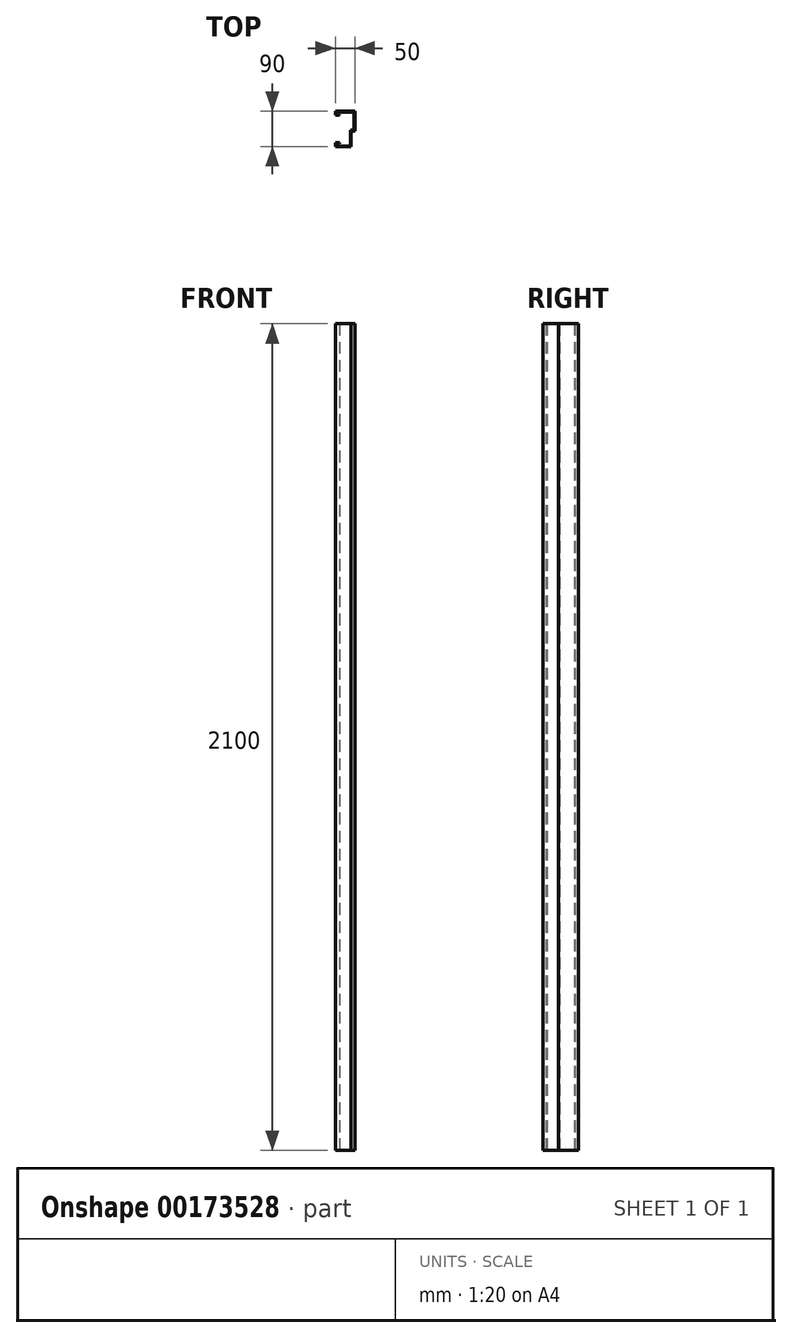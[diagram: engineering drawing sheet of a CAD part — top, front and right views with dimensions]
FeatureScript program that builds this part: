
annotation { "Feature Type Name" : "Feature", "Feature Type Description" : "" }
export const myFeature = defineFeature(function(context is Context, id is Id, definition is map)
    precondition{}
    {
        {
            var Q0;
            Q0=qCreatedBy(makeId("Top.planeOp"),FACE);
            var sketch = newSketch(context, id + "F0", { "sketchPlane" : qUnion([Q0])});
            skLineSegment(sketch, "E0", {"start": v(0, 0) * mm, "end": v(0, -10) * mm});
            skLineSegment(sketch, "E1", {"start": v(0, -10) * mm, "end": v(40, -10) * mm});
            skLineSegment(sketch, "E2", {"start": v(40, -10) * mm, "end": v(40, 30) * mm});
            skLineSegment(sketch, "E3", {"start": v(40, 30) * mm, "end": v(50, 30) * mm});
            skLineSegment(sketch, "E4", {"start": v(50, 30) * mm, "end": v(50, 80) * mm});
            skLineSegment(sketch, "E5", {"start": v(50, 80) * mm, "end": v(0, 80) * mm});
            skLineSegment(sketch, "E6", {"start": v(0, 80) * mm, "end": v(0, 70) * mm});
            skLineSegment(sketch, "E7", {"start": v(0, 0) * mm, "end": v(10, 0) * mm});
            skLineSegment(sketch, "E8", {"start": v(0, 70) * mm, "end": v(10, 70) * mm});
            skLineSegment(sketch, "E9.0", {"start": v(2, 72) * mm, "end": v(10, 72) * mm});
            skLineSegment(sketch, "E10.0", {"start": v(2, 78) * mm, "end": v(2, 72) * mm});
            skLineSegment(sketch, "E11", {"start": v(10, 70) * mm, "end": v(10, 72) * mm});
            skLineSegment(sketch, "E12.0", {"start": v(48, 78) * mm, "end": v(2, 78) * mm});
            skLineSegment(sketch, "E13.0", {"start": v(48, 32) * mm, "end": v(48, 78) * mm});
            skLineSegment(sketch, "E13.1", {"start": v(38, 32) * mm, "end": v(48, 32) * mm});
            skLineSegment(sketch, "E13.2", {"start": v(2, -2) * mm, "end": v(10, -2) * mm});
            skLineSegment(sketch, "E13.3", {"start": v(2, -2) * mm, "end": v(2, -8) * mm});
            skLineSegment(sketch, "E13.4", {"start": v(2, -8) * mm, "end": v(38, -8) * mm});
            skLineSegment(sketch, "E13.5", {"start": v(38, -8) * mm, "end": v(38, 32) * mm});
            skLineSegment(sketch, "E14", {"start": v(10, 0) * mm, "end": v(10, -2) * mm});
            skSolve(sketch);
        }
        {
            var Q0;
            Q0=makeQuery(id+"F0.imprint","IMPRINT",FACE,{"disambiguationData":[TD([[makeQuery(id+"F0.imprint","IMPRINT",EDGE,{"derivedFrom":sQuery(id+"F0.wireOp",EDGE,"E0")}),1.0]])]});
            var Q1;
            Q1=sQuery(id+"F0.wireOp",EDGE,"E2");
            var Q2;
            Q2=sQuery(id+"F0.wireOp",EDGE,"E3");
            var Q3;
            Q3=sQuery(id+"F0.wireOp",EDGE,"E4");
            var Q4;
            Q4=sQuery(id+"F0.wireOp",EDGE,"E5");
            var Q5;
            Q5=sQuery(id+"F0.wireOp",EDGE,"E6");
            var Q6;
            Q6=sQuery(id+"F0.wireOp",EDGE,"E7");
            var Q7;
            Q7=sQuery(id+"F0.wireOp",EDGE,"E8");
            var Q8;
            Q8=sQuery(id+"F0.wireOp",EDGE,"E1");
            var Q9;
            Q9=sQuery(id+"F0.wireOp",EDGE,"E0");
            extrude(context, id + "F1", {"entities" : qUnion([Q0]), "surfaceEntities" : qUnion([Q1, Q2, Q3, Q4, Q5, Q6, Q7, Q8, Q9]), "depth" : 2100 * mm});
        }
    });
